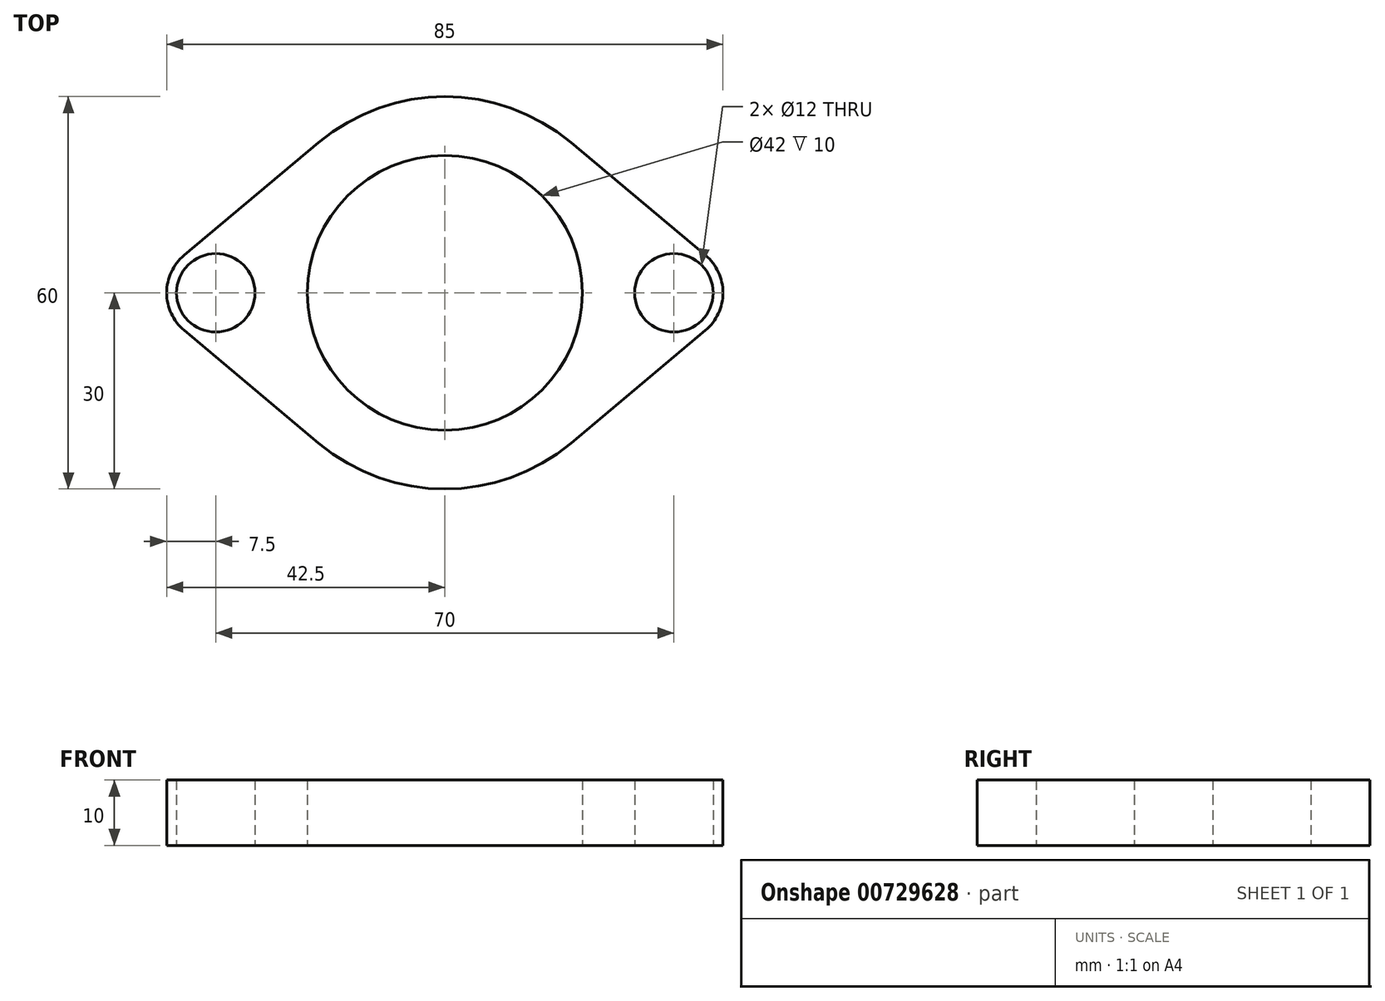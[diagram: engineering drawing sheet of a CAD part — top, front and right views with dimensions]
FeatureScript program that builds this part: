
annotation { "Feature Type Name" : "Feature", "Feature Type Description" : "" }
export const myFeature = defineFeature(function(context is Context, id is Id, definition is map)
    precondition{}
    {
        {
            var Q0;
            Q0=qCreatedBy(makeId("Top.planeOp"),FACE);
            var sketch = newSketch(context, id + "F0", { "sketchPlane" : qUnion([Q0])});
            skArc(sketch, "E0", {"start": v(19.29, 22.98) * mm, "mid": v(0, 30) * mm, "end": v(-19.29, 22.98) * mm});
            skCircle(sketch, "E1", {"center": v(0, 0) * mm, "radius": 21 * mm});
            skCircle(sketch, "E2", {"center": v(35, 0) * mm, "radius": 6 * mm});
            skCircle(sketch, "E3.MirrorC", {"center": v(-35, 0) * mm, "radius": 6 * mm});
            skArc(sketch, "E4", {"start": v(39.82, -5.74) * mm, "mid": v(42.5, 0) * mm, "end": v(39.82, 5.74) * mm});
            skArc(sketch, "E5.MirrorC", {"start": v(-39.82, -5.74) * mm, "mid": v(-42.5, 0) * mm, "end": v(-39.82, 5.74) * mm});
            skLineSegment(sketch, "E6.MirrorCS", {"start": v(-19.29, 22.98) * mm, "end": v(-39.82, 5.74) * mm});
            skLineSegment(sketch, "E7.MirrorCS", {"start": v(-19.29, -22.98) * mm, "end": v(-39.82, -5.74) * mm});
            skLineSegment(sketch, "E8.trimOffspring", {"start": v(19.29, 22.98) * mm, "end": v(39.82, 5.74) * mm});
            skPoint(sketch, "E9.orphan", {"position": v(53.63, 5.85) * mm});
            skPoint(sketch, "E10.orphan", {"position": v(53.63, -5.85) * mm});
            skLineSegment(sketch, "E11.trimOffspring", {"start": v(19.29, -22.98) * mm, "end": v(39.82, -5.74) * mm});
            skPoint(sketch, "E12.MirrorCS.start.orphan", {"position": v(-4.04, -42.55) * mm});
            skPoint(sketch, "E13.orphan", {"position": v(4.04, -42.55) * mm});
            skPoint(sketch, "E14.orphan", {"position": v(4.04, 42.55) * mm});
            skPoint(sketch, "E15.start.orphan", {"position": v(-4.04, 42.55) * mm});
            skArc(sketch, "E16.trimOffspring", {"start": v(-19.29, -22.98) * mm, "mid": v(0, -30) * mm, "end": v(19.29, -22.98) * mm});
            skPoint(sketch, "E17.orphan", {"position": v(-53.63, 5.85) * mm});
            skPoint(sketch, "E18.orphan", {"position": v(-53.63, -5.85) * mm});
            skSolve(sketch);
        }
        {
            var Q0;
            Q0 = qSketchRegion(id + "F0", true);
            extrude(context, id + "F1", {"entities" : qUnion([Q0]), "depth" : 10 * mm, "offsetDistance" : 25 * mm});
        }
    });
